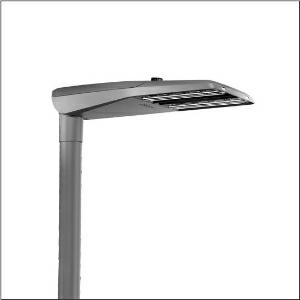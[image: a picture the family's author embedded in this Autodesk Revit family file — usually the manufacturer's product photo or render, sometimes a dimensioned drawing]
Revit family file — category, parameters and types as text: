
# Revit family: streetlight_sl_11_iq_midi___st1_2a_5xc3a41u08me_4bff
name_source: partatom
category: Lighting Fixtures
units: mm (PartAtom-declared; Revit-internal decimal feet)

## family parameters
Cut with Voids When Loaded = No
Host = Face
Light Source = No
Part Type = Normal
Room Calculation Point = No
Round Connector Dimension = Use Diameter
Shared = No

## types (1)
- --- (1 x LED, 18900 lm, 122.6 W, 4000K)
    Apparent Load = 123 VA
    CIE Flux Codes = 32 70 96 100 100
    Color Rendering = 70
    Color Temperature = 4000K
    Default Elevation = 1800 mm
    Description = Streetlight SL 11 iQ midi, mast luminaire, primary light control with 3 zone facetted reflector, of plastic, silver coated, highly specular, primary optical cover: cover, of PMMA, transparent, light distribution: ST1.2a, light emission: direct distribution, primary light characteristic: asymmetric, installation type: post-top, side-entry, LED, High Power LED, rated luminous flux: 18.900lm, luminous efficacy: 154lm/W, light colour: 740, colour temperature: 4000K, control: presetting dimming logarithmic, Street-Remote, Auto-Match, Temp-Guard, Lumen-Switch, Night-Set, Smart-Wire, Light-Fading, Desk-Remote (wireless, voltage-free reading and setting of iQ features in the workshop via application-optimized NFC function/RFID function), optimised constant luminous flux control (CLO 2.0), with cable H07RN-F 5x 1.5mm², mains connection: 220..240V, AC, 50/60Hz, connection cable pre-assembled, cable length: 12,5m, start of lifetime: 123W, end of service life: 130W, reduction: 56W, luminaire housing, of diecast aluminium, powder-coated, Siteco® metallic grey (DB 702S), please order mast flange separately, inclination adjustable without tools: 0°, 5°, 10°, 15° (post-top) | 0°, -5°, -10°, -15° (side-entry), sealing non-destructively replaceable, multi-level sealing system, length: 780mm, width: 376mm, height: 118mm, spigot size: 60/76mm (post-top) and 42/60/76mm (side-entry), mast flange for spigot size: 42mm: 5XC10008XM4, 60mm: 5XC10008XM2, 76/60mm: 5XC10108XM1, equipment: Power, Smart Interface below, protection rating (complete): IP66, insulation class (complete): insulation class II (safety insulation), certification: CE, ENEC in preparation, impact resistance: IK09, permissible operating ambient temperature for outdoor applications: -25..+50°C, standard-compliant lighting for roads and squares, packaging unit: 1 piece

Light Distribution: ST1.2a
    Height = 118 mm
    Lamp = 1 x LED
    Lamp Light Flux = 18900 lm
    Lamp Power = 122.6 W
    Lamp count = 1
    Length = 780 mm
    Luminous efficacy = 154 lm/W
    Manufacturer = Siteco
    ModVariant = No
    Model = 5XC3A41U08ME
    Number of Poles = 1
    OnlyDefault = Yes
    Power Factor = 1
    Product Name = Streetlight SL 11 iQ midi | ST1.2a
    Product group = mast luminaire | pylon top
    ProductGroupID = 6100
    Protection Class = Protection class II
    Protection Degree = IP 66
    RLX_Detail_Level = 1
    RlxData = <blob elided: 69705 chars, md5=657f708a>
    Socket = socket
    Standby Power = 0 W
    System Light Flux = 18900 lm
    System Power = 123 W
    Type Comments = factory setting: luminous flux: 100 % | dim-lin: 254 | 552 mA
    Type Image = l_1005968.jpg
    URL = http://relux.com
    VarID = @adj_043505
    Voltage = 0 V
    Weight = 0.00 kg
    Width = 376 mm

## geometry (parser evidence)
native form markers: Blend x4, Sweep x10
no freeform markers — native parametric forms only
